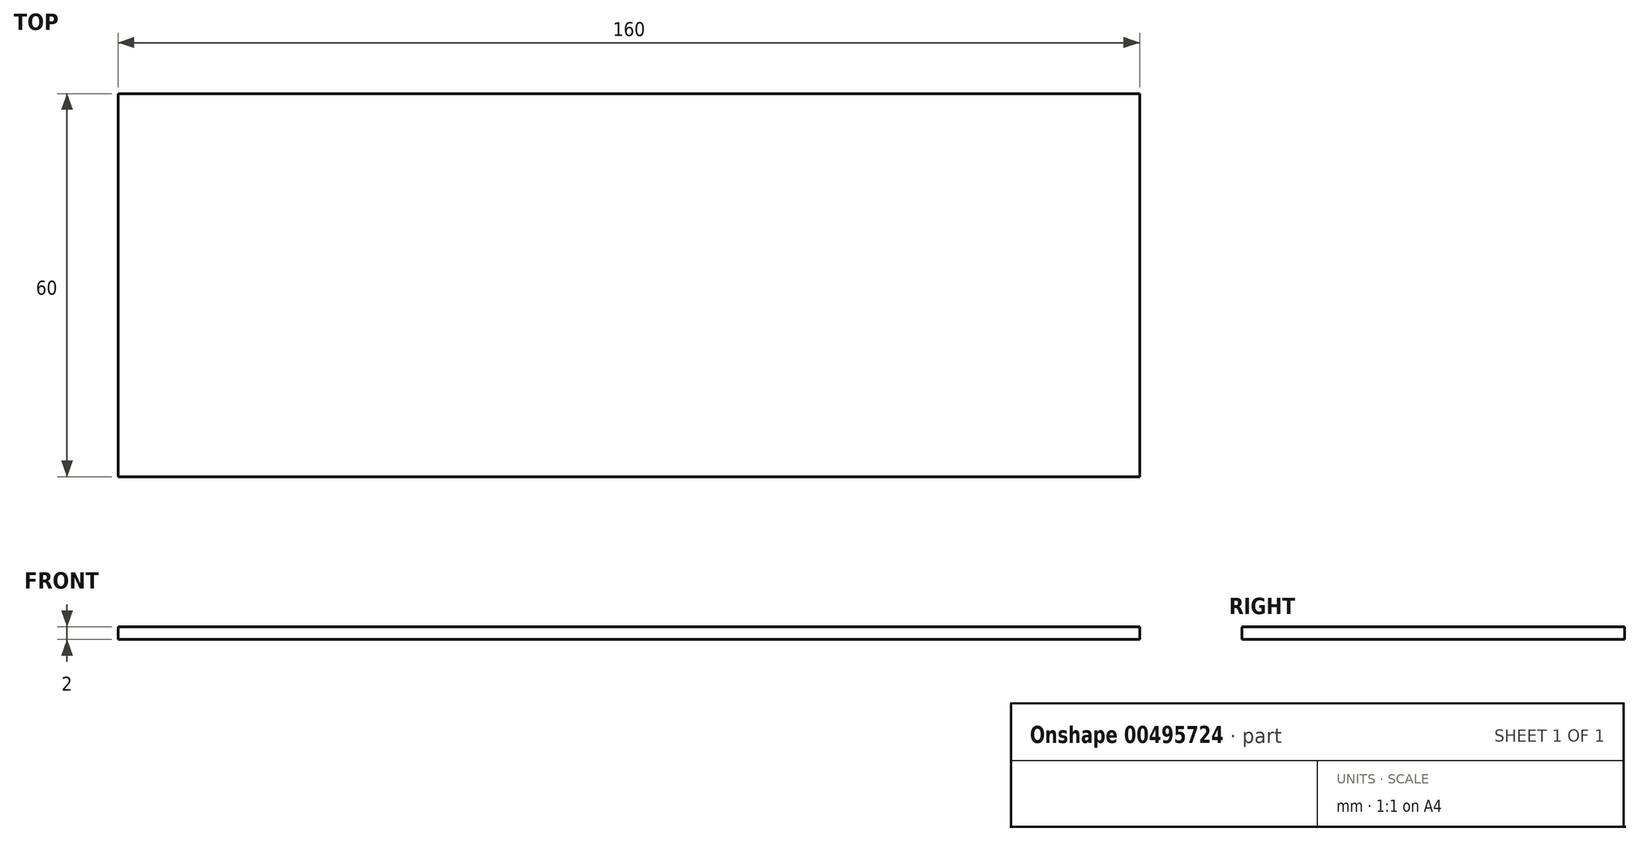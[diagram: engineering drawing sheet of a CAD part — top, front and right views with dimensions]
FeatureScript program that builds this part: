
annotation { "Feature Type Name" : "Feature", "Feature Type Description" : "" }
export const myFeature = defineFeature(function(context is Context, id is Id, definition is map)
    precondition{}
    {
        {
            var Q0;
            Q0=qCreatedBy(makeId("Top.planeOp"),FACE);
            var sketch = newSketch(context, id + "F0", { "sketchPlane" : qUnion([Q0])});
            skLineSegment(sketch, "E0.bottom", {"start": v(0, 0) * mm, "end": v(160, 0) * mm});
            skLineSegment(sketch, "E0.top", {"start": v(0, 60) * mm, "end": v(160, 60) * mm});
            skLineSegment(sketch, "E0.left", {"start": v(0, 0) * mm, "end": v(0, 60) * mm});
            skLineSegment(sketch, "E0.right", {"start": v(160, 0) * mm, "end": v(160, 60) * mm});
            skSolve(sketch);
        }
        {
            var Q0;
            Q0 = qSketchRegion(id + "F0", true);
            extrude(context, id + "F1", {"entities" : qUnion([Q0]), "depth" : 2 * mm});
        }
    });
